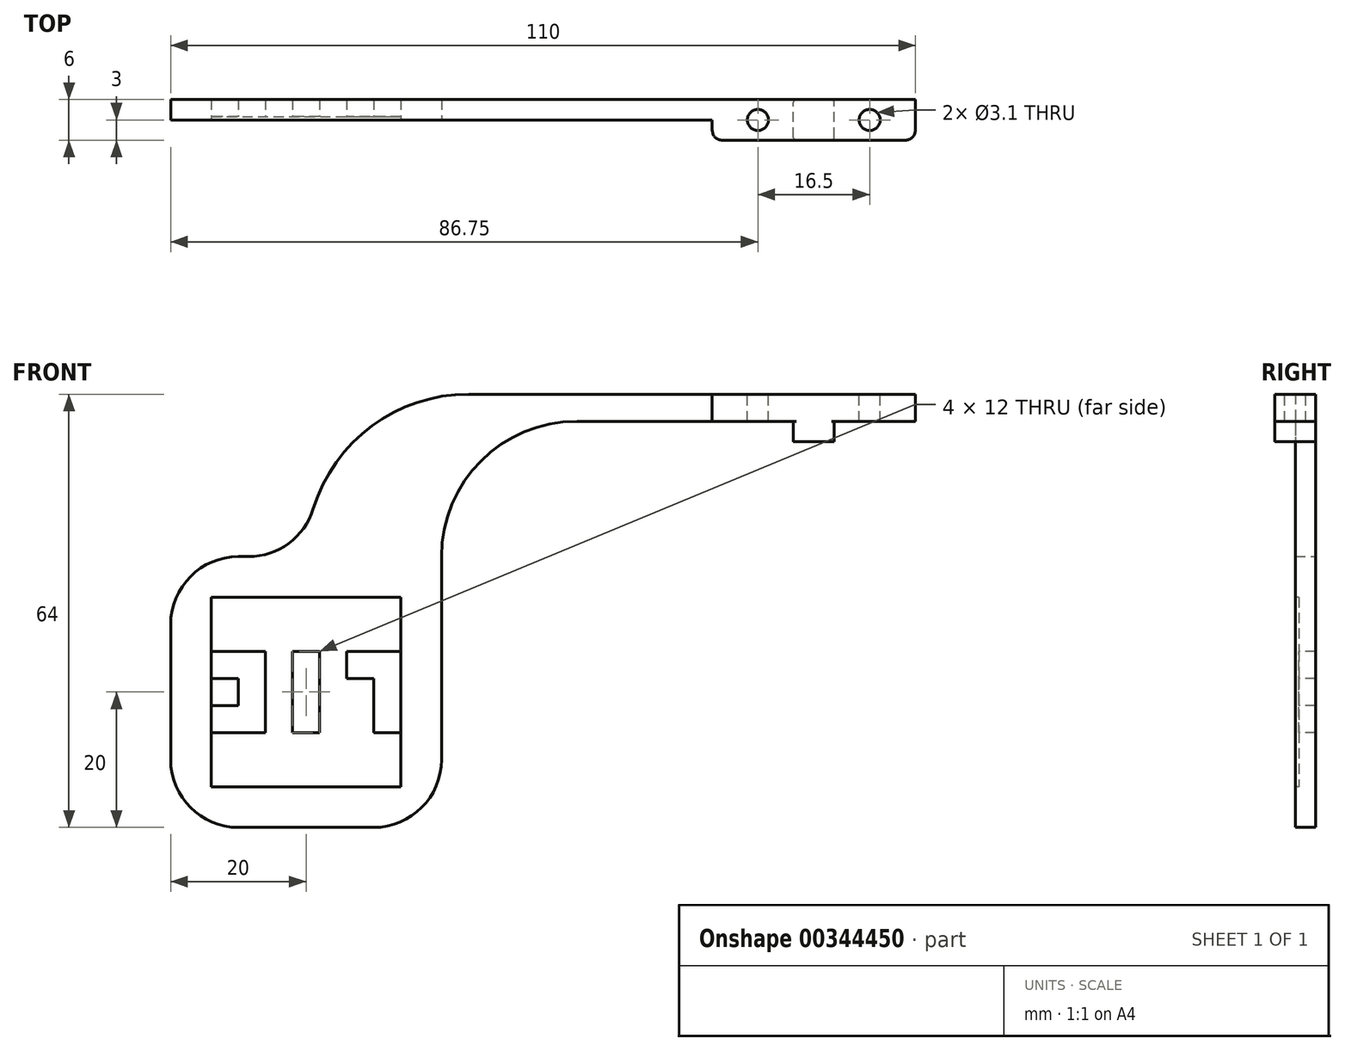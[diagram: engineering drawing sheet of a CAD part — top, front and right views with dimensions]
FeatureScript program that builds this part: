
annotation { "Feature Type Name" : "Feature", "Feature Type Description" : "" }
export const myFeature = defineFeature(function(context is Context, id is Id, definition is map)
    precondition{}
    {
        {
            var Q0;
            Q0=qCreatedBy(makeId("Top.planeOp"),FACE);
            var sketch = newSketch(context, id + "F0", { "sketchPlane" : qUnion([Q0])});
            skLineSegment(sketch, "E0.bottom", {"start": v(-15, 3) * mm, "end": v(15, 3) * mm});
            skLineSegment(sketch, "E0.top", {"start": v(-15, -3) * mm, "end": v(15, -3) * mm});
            skLineSegment(sketch, "E0.left", {"start": v(-15, 3) * mm, "end": v(-15, -3) * mm});
            skLineSegment(sketch, "E0.right", {"start": v(15, 3) * mm, "end": v(15, -3) * mm});
            skPoint(sketch, "E1", {"position": v(0, 3) * mm});
            skPoint(sketch, "E2", {"position": v(-15, 0) * mm});
            skSolve(sketch);
        }
        {
            var Q0;
            Q0=makeQuery(id+"F0.imprint","IMPRINT",FACE,{"disambiguationData":[TD([[makeQuery(id+"F0.imprint","IMPRINT",EDGE,{"derivedFrom":sQuery(id+"F0.wireOp",EDGE,"E0.bottom")}),-1.0]])]});
            extrude(context, id + "F1", {"entities" : qUnion([Q0]), "depth" : 4 * mm});
        }
        {
            var Q0;
            Q0=makeQuery(id+"F1.opExtrude","CAP_FACE",FACE,{"disambiguationData":[OSD([sQuery(id+"F0.wireOp",EDGE,"E0.bottom"),sQuery(id+"F0.wireOp",EDGE,"E0.top"),sQuery(id+"F0.wireOp",EDGE,"E0.left"),sQuery(id+"F0.wireOp",EDGE,"E0.right")])],"isStart":true});
            var sketch = newSketch(context, id + "F2", { "sketchPlane" : qUnion([Q0])});
            skLineSegment(sketch, "E3.bottom", {"start": v(-3, 3) * mm, "end": v(3, 3) * mm});
            skLineSegment(sketch, "E3.top", {"start": v(-3, -3) * mm, "end": v(3, -3) * mm});
            skLineSegment(sketch, "E3.left", {"start": v(-3, 3) * mm, "end": v(-3, -3) * mm});
            skLineSegment(sketch, "E3.right", {"start": v(3, 3) * mm, "end": v(3, -3) * mm});
            skPoint(sketch, "E4", {"position": v(0, 3) * mm});
            skSolve(sketch);
        }
        {
            var Q0;
            Q0=makeQuery(id+"F2.imprint","IMPRINT",FACE,{"disambiguationData":[TD([[makeQuery(id+"F2.imprint","IMPRINT",EDGE,{"derivedFrom":sQuery(id+"F2.wireOp",EDGE,"E3.bottom")}),-1.0]])]});
            extrude(context, id + "F3", {"entities" : qUnion([Q0]), "operationType" : NewBodyOperationType.ADD, "depth" : 3 * mm});
        }
        {
            var Q0;
            Q0=makeQuery(id+"F1.opExtrude","CAP_FACE",FACE,{"disambiguationData":[OSD([sQuery(id+"F0.wireOp",EDGE,"E0.bottom"),sQuery(id+"F0.wireOp",EDGE,"E0.top"),sQuery(id+"F0.wireOp",EDGE,"E0.left"),sQuery(id+"F0.wireOp",EDGE,"E0.right")])],"isStart":false});
            var sketch = newSketch(context, id + "F4", { "sketchPlane" : qUnion([Q0])});
            skCircle(sketch, "E5", {"center": v(-8.25, 0) * mm, "radius": 1.55 * mm});
            skCircle(sketch, "E6", {"center": v(8.25, 0) * mm, "radius": 1.55 * mm});
            skLineSegment(sketch, "E7", {"start": v(-8.25, 0) * mm, "end": v(8.25, 0) * mm, "construction": true});
            skPoint(sketch, "E8", {"position": v(0, 0) * mm});
            skSolve(sketch);
        }
        {
            var Q0;
            Q0=makeQuery(id+"F4.imprint","IMPRINT",FACE,{"disambiguationData":[TD([[makeQuery(id+"F4.imprint","IMPRINT",EDGE,{"derivedFrom":sQuery(id+"F4.wireOp",EDGE,"E5")}),1.0]])]});
            var Q1;
            Q1=makeQuery(id+"F4.imprint","IMPRINT",FACE,{"disambiguationData":[TD([[makeQuery(id+"F4.imprint","IMPRINT",EDGE,{"derivedFrom":sQuery(id+"F4.wireOp",EDGE,"E6")}),1.0]])]});
            extrude(context, id + "F5", {"entities" : qUnion([Q0, Q1]), "operationType" : NewBodyOperationType.REMOVE, "endBound" : BoundingType.UP_TO_NEXT, "oppositeDirection" : true, "depth" : 25 * mm});
        }
        {
            var Q0;
            Q0=qCreatedBy(makeId("Front.planeOp"),FACE);
            var sketch = newSketch(context, id + "F6", { "sketchPlane" : qUnion([Q0])});
            skLineSegment(sketch, "E9.0.0", {"start": v(-15, 0) * mm, "end": v(-3, 0) * mm, "construction": true});
            skLineSegment(sketch, "E9.0.1", {"start": v(-3, 0) * mm, "end": v(-3, -3) * mm, "construction": true});
            skLineSegment(sketch, "E9.0.2", {"start": v(-3, -3) * mm, "end": v(3, -3) * mm, "construction": true});
            skLineSegment(sketch, "E9.0.3", {"start": v(3, -3) * mm, "end": v(3, 0) * mm, "construction": true});
            skLineSegment(sketch, "E9.0.4", {"start": v(3, 0) * mm, "end": v(15, 0) * mm, "construction": true});
            skLineSegment(sketch, "E9.0.5", {"start": v(15, 0) * mm, "end": v(15, 4) * mm, "construction": true});
            skLineSegment(sketch, "E9.0.6", {"start": v(15, 4) * mm, "end": v(-15, 4) * mm, "construction": true});
            skLineSegment(sketch, "E9.0.7", {"start": v(-15, 4) * mm, "end": v(-15, 0) * mm, "construction": true});
            skLineSegment(sketch, "E10", {"start": v(-15, 4) * mm, "end": v(-51, 4) * mm});
            skArc(sketch, "E11", {"start": v(-51, 4) * mm, "mid": v(-67.97, -3.03) * mm, "end": v(-75, -20) * mm});
            skArc(sketch, "E12", {"start": v(-35, 0) * mm, "mid": v(-49.14, -5.86) * mm, "end": v(-55, -20) * mm});
            skLineSegment(sketch, "E13", {"start": v(-35, 0) * mm, "end": v(-15, 0) * mm});
            skLineSegment(sketch, "E14", {"start": v(-75, -20) * mm, "end": v(-95, -20) * mm});
            skLineSegment(sketch, "E15", {"start": v(-95, -20) * mm, "end": v(-95, -60) * mm});
            skLineSegment(sketch, "E16", {"start": v(-95, -60) * mm, "end": v(-55, -60) * mm});
            skLineSegment(sketch, "E17", {"start": v(-55, -60) * mm, "end": v(-55, -20) * mm});
            skLineSegment(sketch, "E18", {"start": v(-15, 4) * mm, "end": v(-15, 0) * mm});
            skSolve(sketch);
        }
        {
            var Q0;
            Q0=makeQuery(id+"F6.imprint","IMPRINT",FACE,{"disambiguationData":[TD([[makeQuery(id+"F6.imprint","IMPRINT",EDGE,{"derivedFrom":sQuery(id+"F6.wireOp",EDGE,"E10")}),1.0]])]});
            var Q1;
            Q1=makeQuery(id+"F3.boolean.opBoolean","MERGE",FACE,{"derivedFrom":[makeQuery(id+"F1.opExtrude","SWEPT_FACE",FACE,{"disambiguationData":[OSD([sQuery(id+"F0.wireOp",EDGE,"E0.bottom")])]}),makeQuery(id+"F3.opExtrude","SWEPT_FACE",FACE,{"disambiguationData":[OSD([sQuery(id+"F2.wireOp",EDGE,"E3.top")])]})]});
            extrude(context, id + "F7", {"entities" : qUnion([Q0]), "operationType" : NewBodyOperationType.ADD, "endBound" : BoundingType.UP_TO_SURFACE, "oppositeDirection" : true, "endBoundEntityFace" : qUnion([Q1]), "depth" : 25 * mm});
        }
        {
            var Q0;
            Q0=makeQuery(id+"F7.opExtrude","CAP_FACE",FACE,{"disambiguationData":[OSD([sQuery(id+"F6.wireOp",EDGE,"E10"),sQuery(id+"F6.wireOp",EDGE,"E11"),sQuery(id+"F6.wireOp",EDGE,"E12"),sQuery(id+"F6.wireOp",EDGE,"E13"),sQuery(id+"F6.wireOp",EDGE,"E14"),sQuery(id+"F6.wireOp",EDGE,"E15"),sQuery(id+"F6.wireOp",EDGE,"E16"),sQuery(id+"F6.wireOp",EDGE,"E17"),sQuery(id+"F6.wireOp",EDGE,"E18")])],"isStart":true});
            var sketch = newSketch(context, id + "F8", { "sketchPlane" : qUnion([Q0])});
            skLineSegment(sketch, "E19.bottom", {"start": v(-89, -26) * mm, "end": v(-61, -26) * mm});
            skLineSegment(sketch, "E19.top", {"start": v(-89, -54) * mm, "end": v(-61, -54) * mm});
            skLineSegment(sketch, "E19.left", {"start": v(-89, -26) * mm, "end": v(-89, -54) * mm});
            skLineSegment(sketch, "E19.right", {"start": v(-61, -26) * mm, "end": v(-61, -54) * mm});
            skPoint(sketch, "E20", {"position": v(-75, -26) * mm});
            skPoint(sketch, "E21", {"position": v(-61, -40) * mm});
            skPoint(sketch, "E22", {"position": v(-95, -40) * mm});
            skPoint(sketch, "E23", {"position": v(-75, -60) * mm});
            skSolve(sketch);
        }
        {
            var Q0;
            Q0=makeQuery(id+"F8.imprint","IMPRINT",FACE,{"disambiguationData":[TD([[makeQuery(id+"F8.imprint","IMPRINT",EDGE,{"derivedFrom":sQuery(id+"F8.wireOp",EDGE,"E19.bottom")}),-1.0]])]});
            extrude(context, id + "F9", {"entities" : qUnion([Q0]), "operationType" : NewBodyOperationType.REMOVE, "oppositeDirection" : true, "depth" : 0.5 * mm});
        }
        {
            var Q0;
            Q0=makeQuery(id+"F9.boolean.opBoolean","COPY",FACE,{"derivedFrom":makeQuery(id+"F9.opExtrude","CAP_FACE",FACE,{"disambiguationData":[OSD([sQuery(id+"F8.wireOp",EDGE,"E19.bottom"),sQuery(id+"F8.wireOp",EDGE,"E19.top"),sQuery(id+"F8.wireOp",EDGE,"E19.left"),sQuery(id+"F8.wireOp",EDGE,"E19.right")])],"isStart":false})});
            var sketch = newSketch(context, id + "F10", { "sketchPlane" : qUnion([Q0])});
            skPoint(sketch, "E24", {"position": v(-89, -26) * mm});
            skPoint(sketch, "E25", {"position": v(-61, -26) * mm});
            skPoint(sketch, "E26", {"position": v(-61, -54) * mm});
            skLineSegment(sketch, "E27", {"start": v(-89, -26) * mm, "end": v(-85, -26) * mm, "construction": true});
            skLineSegment(sketch, "E28", {"start": v(-85, -26) * mm, "end": v(-81, -26) * mm, "construction": true});
            skLineSegment(sketch, "E29", {"start": v(-81, -26) * mm, "end": v(-77, -26) * mm, "construction": true});
            skLineSegment(sketch, "E30", {"start": v(-77, -26) * mm, "end": v(-73, -26) * mm, "construction": true});
            skLineSegment(sketch, "E31", {"start": v(-73, -26) * mm, "end": v(-69, -26) * mm, "construction": true});
            skLineSegment(sketch, "E32", {"start": v(-61, -26) * mm, "end": v(-61, -30) * mm, "construction": true});
            skLineSegment(sketch, "E33", {"start": v(-61, -30) * mm, "end": v(-61, -34) * mm, "construction": true});
            skLineSegment(sketch, "E34", {"start": v(-61, -34) * mm, "end": v(-61, -38) * mm, "construction": true});
            skLineSegment(sketch, "E35", {"start": v(-61, -38) * mm, "end": v(-61, -42) * mm, "construction": true});
            skLineSegment(sketch, "E36", {"start": v(-61, -42) * mm, "end": v(-61, -46) * mm, "construction": true});
            skLineSegment(sketch, "E37", {"start": v(-69, -26) * mm, "end": v(-65, -26) * mm, "construction": true});
            skLineSegment(sketch, "E38", {"start": v(-65, -26) * mm, "end": v(-61, -26) * mm, "construction": true});
            skLineSegment(sketch, "E39", {"start": v(-61, -46) * mm, "end": v(-61, -50) * mm, "construction": true});
            skLineSegment(sketch, "E40", {"start": v(-61, -50) * mm, "end": v(-61, -54) * mm, "construction": true});
            skLineSegment(sketch, "E41", {"start": v(-89, -34) * mm, "end": v(-81, -34) * mm});
            skLineSegment(sketch, "E42", {"start": v(-81, -34) * mm, "end": v(-81, -46) * mm});
            skLineSegment(sketch, "E43", {"start": v(-81, -46) * mm, "end": v(-89, -46) * mm});
            skLineSegment(sketch, "E44", {"start": v(-89, -46) * mm, "end": v(-89, -42) * mm});
            skLineSegment(sketch, "E45", {"start": v(-89, -42) * mm, "end": v(-85, -42) * mm});
            skLineSegment(sketch, "E46", {"start": v(-85, -42) * mm, "end": v(-85, -38) * mm});
            skLineSegment(sketch, "E47", {"start": v(-85, -38) * mm, "end": v(-89, -38) * mm});
            skLineSegment(sketch, "E48", {"start": v(-89, -38) * mm, "end": v(-89, -34) * mm});
            skLineSegment(sketch, "E49", {"start": v(-77, -34) * mm, "end": v(-77, -46) * mm});
            skLineSegment(sketch, "E50", {"start": v(-77, -46) * mm, "end": v(-73, -46) * mm});
            skLineSegment(sketch, "E51", {"start": v(-73, -46) * mm, "end": v(-73, -34) * mm});
            skLineSegment(sketch, "E52", {"start": v(-73, -34) * mm, "end": v(-77, -34) * mm});
            skLineSegment(sketch, "E53", {"start": v(-61, -34) * mm, "end": v(-69, -34) * mm});
            skLineSegment(sketch, "E54", {"start": v(-69, -34) * mm, "end": v(-69, -38) * mm});
            skLineSegment(sketch, "E55", {"start": v(-69, -38) * mm, "end": v(-65, -38) * mm});
            skLineSegment(sketch, "E56", {"start": v(-65, -38) * mm, "end": v(-65, -46) * mm});
            skLineSegment(sketch, "E57", {"start": v(-65, -46) * mm, "end": v(-61, -46) * mm});
            skLineSegment(sketch, "E58", {"start": v(-61, -46) * mm, "end": v(-61, -34) * mm});
            skSolve(sketch);
        }
        {
            var Q0;
            Q0=makeQuery(id+"F7.opExtrude","CAP_EDGE",EDGE,{"disambiguationData":[OSD([sQuery(id+"F6.wireOp",EDGE,"E18")])],"isStart":true});
            var Q1;
            Q1=makeQuery(id+"F1.opExtrude","SWEPT_EDGE",EDGE,{"disambiguationData":[OSD([sQuery(id+"F0.wireOp",EDGE,"E0.top"),sQuery(id+"F0.wireOp",EDGE,"E0.left")])]});
            var Q2;
            Q2=makeQuery(id+"F1.opExtrude","SWEPT_EDGE",EDGE,{"disambiguationData":[OSD([sQuery(id+"F0.wireOp",EDGE,"E0.top"),sQuery(id+"F0.wireOp",EDGE,"E0.right")])]});
            fillet(context, id + "F11", {"entities" : qUnion([Q0, Q1, Q2]), "radius" : 1.5 * mm, "tangentPropagation" : true, "allowEdgeOverflow" : false});
        }
        {
            var Q0;
            Q0=makeQuery(id+"F7.opExtrude","SWEPT_EDGE",EDGE,{"disambiguationData":[OSD([sQuery(id+"F6.wireOp",EDGE,"E16"),sQuery(id+"F6.wireOp",EDGE,"E17")])]});
            var Q1;
            Q1=makeQuery(id+"F7.opExtrude","SWEPT_EDGE",EDGE,{"disambiguationData":[OSD([sQuery(id+"F6.wireOp",EDGE,"E15"),sQuery(id+"F6.wireOp",EDGE,"E16")])]});
            var Q2;
            Q2=makeQuery(id+"F7.opExtrude","SWEPT_EDGE",EDGE,{"disambiguationData":[OSD([sQuery(id+"F6.wireOp",EDGE,"E14"),sQuery(id+"F6.wireOp",EDGE,"E15")])]});
            var Q3;
            Q3=makeQuery(id+"F7.opExtrude","SWEPT_EDGE",EDGE,{"disambiguationData":[OSD([sQuery(id+"F6.wireOp",EDGE,"E11"),sQuery(id+"F6.wireOp",EDGE,"E14")])]});
            fillet(context, id + "F12", {"entities" : qUnion([Q0, Q1, Q2, Q3]), "radius" : 10 * mm, "tangentPropagation" : true, "allowEdgeOverflow" : false});
        }
        {
            var Q0;
            Q0=makeQuery(id+"F3.opExtrude","SWEPT_EDGE",EDGE,{"disambiguationData":[OSD([sQuery(id+"F0.wireOp",EDGE,"E0.top"),sQuery(id+"F2.wireOp",EDGE,"E3.bottom"),sQuery(id+"F2.wireOp",EDGE,"E3.right")])]});
            var Q1;
            Q1=makeQuery(id+"F3.opExtrude","SWEPT_EDGE",EDGE,{"disambiguationData":[OSD([sQuery(id+"F0.wireOp",EDGE,"E0.bottom"),sQuery(id+"F2.wireOp",EDGE,"E3.top"),sQuery(id+"F2.wireOp",EDGE,"E3.right")])]});
            var Q2;
            Q2=makeQuery(id+"F3.opExtrude","SWEPT_EDGE",EDGE,{"disambiguationData":[OSD([sQuery(id+"F0.wireOp",EDGE,"E0.bottom"),sQuery(id+"F2.wireOp",EDGE,"E3.top"),sQuery(id+"F2.wireOp",EDGE,"E3.left")])]});
            var Q3;
            Q3=makeQuery(id+"F3.opExtrude","SWEPT_EDGE",EDGE,{"disambiguationData":[OSD([sQuery(id+"F0.wireOp",EDGE,"E0.top"),sQuery(id+"F2.wireOp",EDGE,"E3.bottom"),sQuery(id+"F2.wireOp",EDGE,"E3.left")])]});
            fillet(context, id + "F13", {"entities" : qUnion([Q0, Q1, Q2, Q3]), "radius" : 0.4 * mm, "tangentPropagation" : true, "allowEdgeOverflow" : false});
        }
        {
            var Q0;
            Q0 = qSketchRegion(id + "F10", true);
            extrude(context, id + "F14", {"entities" : qUnion([Q0]), "operationType" : NewBodyOperationType.REMOVE, "endBound" : BoundingType.UP_TO_NEXT, "oppositeDirection" : true, "depth" : 25 * mm});
        }
    });
